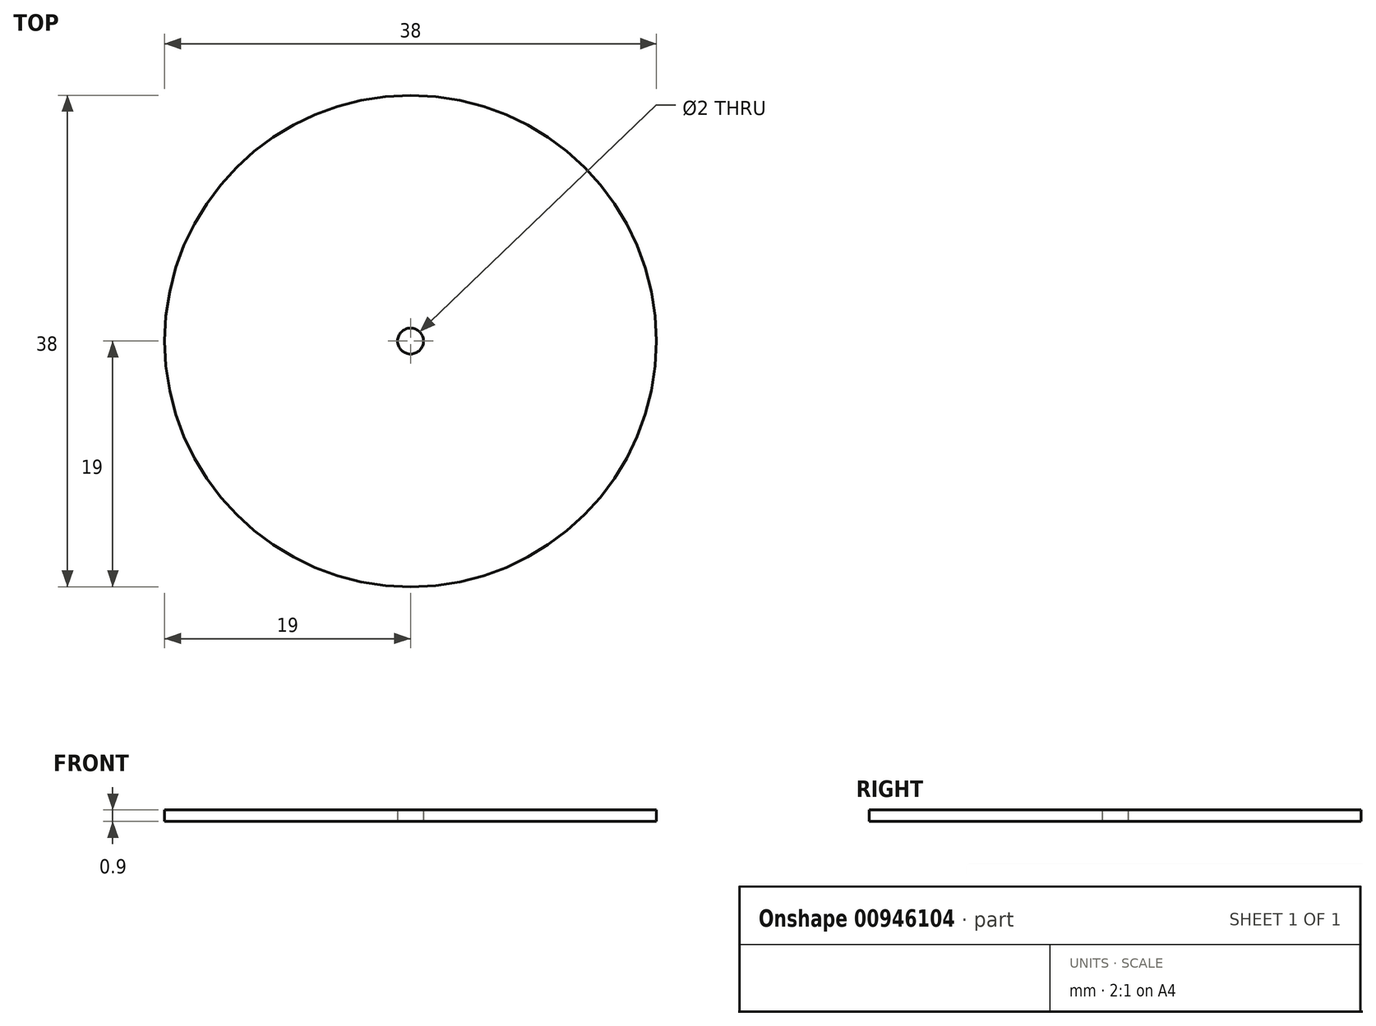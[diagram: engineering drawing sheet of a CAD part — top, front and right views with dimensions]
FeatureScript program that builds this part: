
annotation { "Feature Type Name" : "Feature", "Feature Type Description" : "" }
export const myFeature = defineFeature(function(context is Context, id is Id, definition is map)
    precondition{}
    {
        {
            var Q0;
            Q0=qCreatedBy(makeId("Top.planeOp"),FACE);
            var sketch = newSketch(context, id + "F0", { "sketchPlane" : qUnion([Q0])});
            skCircle(sketch, "E0", {"center": v(0, 0) * mm, "radius": 19 * mm});
            skCircle(sketch, "E1", {"center": v(0, 0) * mm, "radius": 1 * mm});
            skSolve(sketch);
        }
        {
            var Q0;
            Q0=makeQuery(id+"F0.imprint","IMPRINT",FACE,{"disambiguationData":[TD([[makeQuery(id+"F0.imprint","IMPRINT",EDGE,{"derivedFrom":sQuery(id+"F0.wireOp",EDGE,"E0")}),1.0]])]});
            extrude(context, id + "F1", {"entities" : qUnion([Q0]), "depth" : .9 * mm, "offsetDistance" : 25 * mm});
        }
    });
